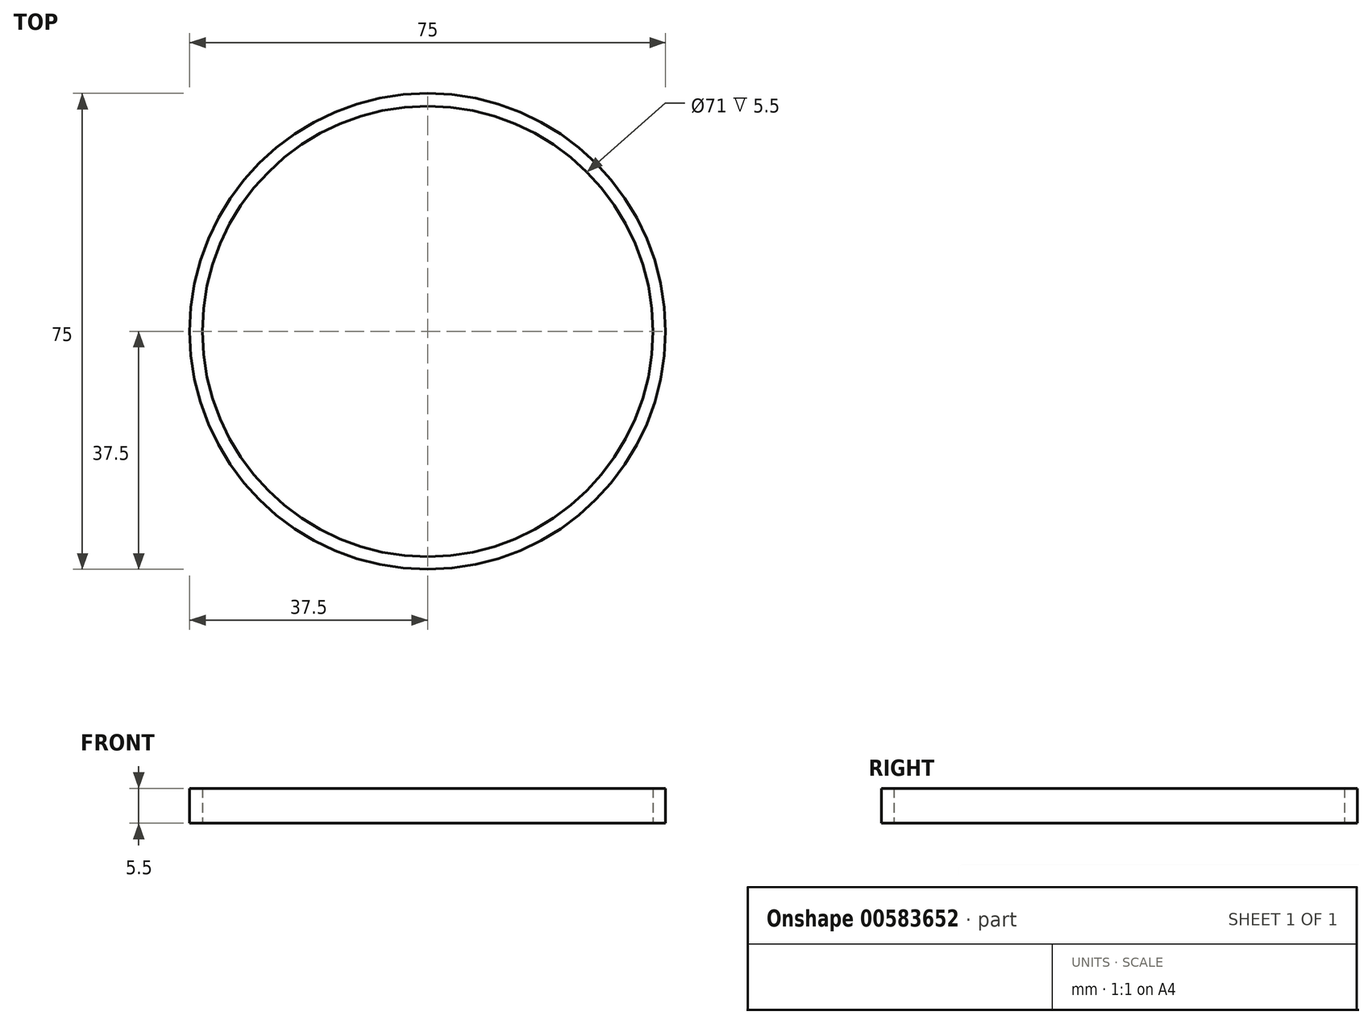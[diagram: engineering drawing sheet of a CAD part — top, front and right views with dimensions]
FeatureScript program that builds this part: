
annotation { "Feature Type Name" : "Feature", "Feature Type Description" : "" }
export const myFeature = defineFeature(function(context is Context, id is Id, definition is map)
    precondition{}
    {
        {
            var Q0;
            Q0=qCreatedBy(makeId("Top.planeOp"),FACE);
            var sketch = newSketch(context, id + "F0", { "sketchPlane" : qUnion([Q0])});
            skCircle(sketch, "E0", {"center": v(0, 0) * mm, "radius": 35.5 * mm});
            skCircle(sketch, "E1", {"center": v(0, 0) * mm, "radius": 37.5 * mm});
            skSolve(sketch);
        }
        {
            var Q0;
            Q0=qSketchRegion(id+"F0",true);
            extrude(context, id + "F1", {"entities" : qUnion([Q0]), "depth" : 5.5 * mm, "offsetDistance" : 25 * mm});
        }
    });
